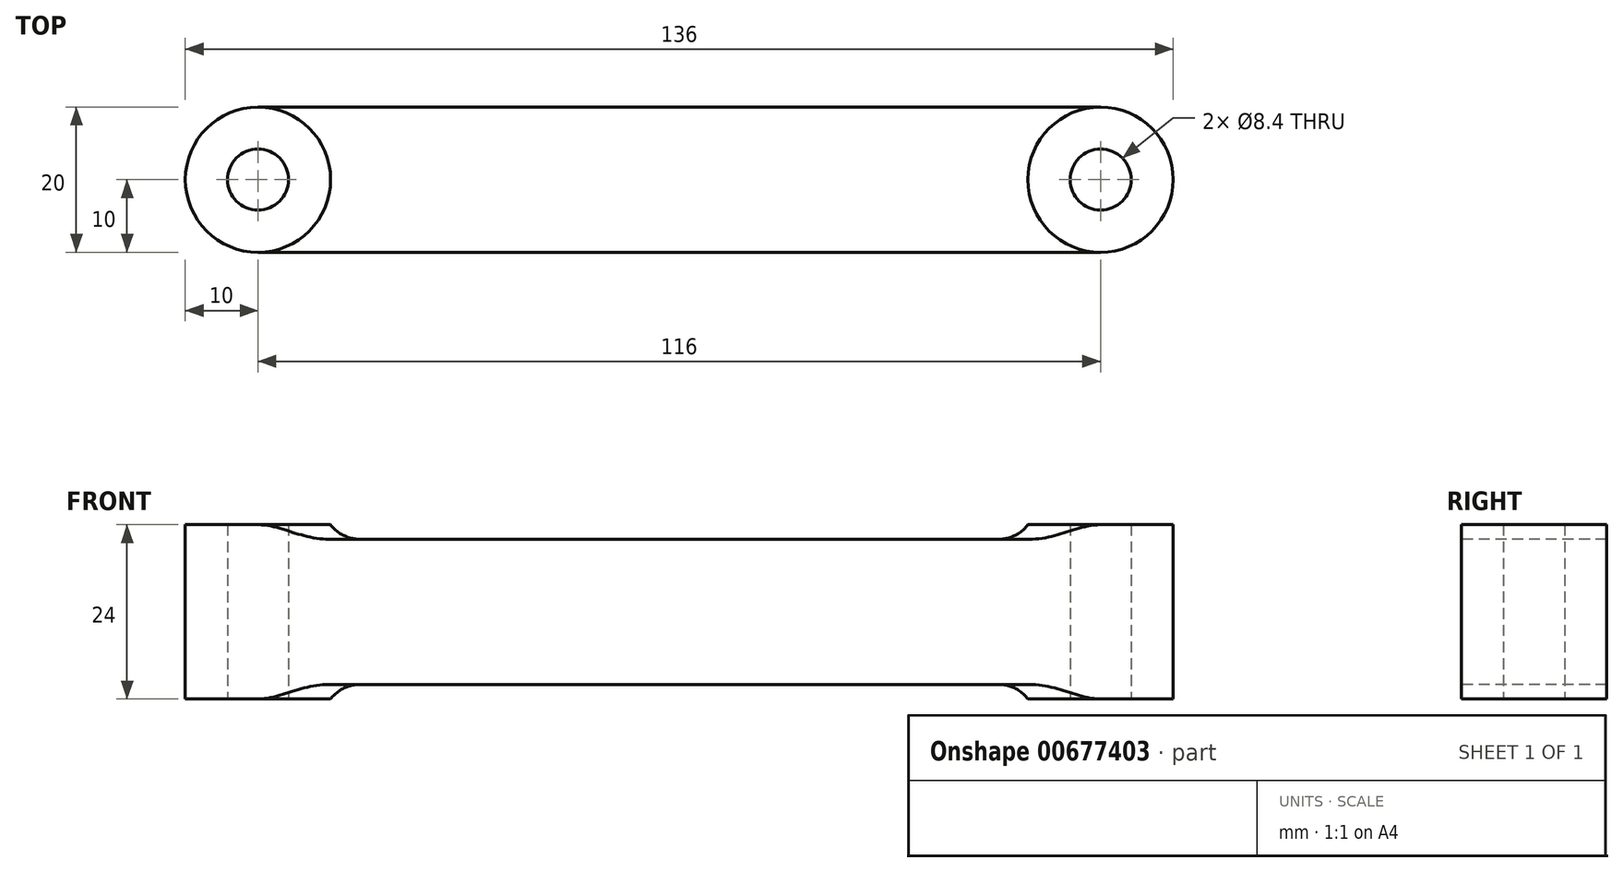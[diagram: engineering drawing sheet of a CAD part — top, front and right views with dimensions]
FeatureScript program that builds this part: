
annotation { "Feature Type Name" : "Feature", "Feature Type Description" : "" }
export const myFeature = defineFeature(function(context is Context, id is Id, definition is map)
    precondition{}
    {
        {
            var Q0;
            Q0=qCreatedBy(makeId("Top.planeOp"),FACE);
            var sketch = newSketch(context, id + "F0", { "sketchPlane" : qUnion([Q0])});
            skLineSegment(sketch, "E0.bottom", {"start": v(58, -10) * mm, "end": v(-58, -10) * mm});
            skLineSegment(sketch, "E0.top", {"start": v(58, 10) * mm, "end": v(-58, 10) * mm});
            skPoint(sketch, "E0.middle", {"position": v(0, 0) * mm});
            skCircle(sketch, "E1", {"center": v(-58, 0) * mm, "radius": 4.2 * mm});
            skPoint(sketch, "E1.centerSnap0", {"position": v(-68, 0) * mm});
            skCircle(sketch, "E2", {"center": v(58, 0) * mm, "radius": 4.2 * mm});
            skPoint(sketch, "E2.centerSnap0", {"position": v(68, 0) * mm});
            skArc(sketch, "E3", {"start": v(-58, 10) * mm, "mid": v(-68, 0) * mm, "end": v(-58, -10) * mm});
            skArc(sketch, "E4", {"start": v(58, -10) * mm, "mid": v(68, 0) * mm, "end": v(58, 10) * mm});
            skSolve(sketch);
        }
        {
            var Q0;
            Q0=makeQuery(id+"F0.imprint","IMPRINT",FACE,{"disambiguationData":[TD([[makeQuery(id+"F0.imprint","IMPRINT",EDGE,{"derivedFrom":sQuery(id+"F0.wireOp",EDGE,"E0.bottom")}),-1.0]])]});
            extrude(context, id + "F1", {"entities" : qUnion([Q0]), "depth" : 20 * mm, "offsetDistance" : 25 * mm});
        }
        {
            var Q0;
            Q0=makeQuery(id+"F1.opExtrude","CAP_FACE",FACE,{"disambiguationData":[OSD([sQuery(id+"F0.wireOp",EDGE,"E0.bottom"),sQuery(id+"F0.wireOp",EDGE,"E0.top"),sQuery(id+"F0.wireOp",EDGE,"E1"),sQuery(id+"F0.wireOp",EDGE,"E2"),sQuery(id+"F0.wireOp",EDGE,"E3"),sQuery(id+"F0.wireOp",EDGE,"E4")])],"isStart":false});
            var sketch = newSketch(context, id + "F2", { "sketchPlane" : qUnion([Q0])});
            skCircle(sketch, "E5", {"center": v(-58, 0) * mm, "radius": 10 * mm});
            skCircle(sketch, "E6", {"center": v(58, 0) * mm, "radius": 10 * mm});
            skCircle(sketch, "E7.0", {"center": v(-58, 0) * mm, "radius": 4.2 * mm});
            skCircle(sketch, "E8.0", {"center": v(58, 0) * mm, "radius": 4.2 * mm});
            skSolve(sketch);
        }
        {
            var Q0;
            Q0 = qSketchRegion(id + "F2", true);
            extrude(context, id + "F3", {"entities" : qUnion([Q0]), "operationType" : NewBodyOperationType.ADD, "depth" : 2 * mm, "offsetDistance" : 25 * mm, "hasSecondDirection" : true, "secondDirectionOppositeDirection" : true, "secondDirectionDepth" : 22 * mm});
        }
        {
            var Q0;
            Q0=makeQuery(id+"F3.boolean.opBoolean","INTERSECT",EDGE,{"derivedFrom":[makeQuery(id+"F1.opExtrude","CAP_FACE",FACE,{"disambiguationData":[OSD([sQuery(id+"F0.wireOp",EDGE,"E0.bottom"),sQuery(id+"F0.wireOp",EDGE,"E0.top"),sQuery(id+"F0.wireOp",EDGE,"E1"),sQuery(id+"F0.wireOp",EDGE,"E2"),sQuery(id+"F0.wireOp",EDGE,"E3"),sQuery(id+"F0.wireOp",EDGE,"E4")])],"isStart":false}),makeQuery(id+"F3.opExtrude","SWEPT_FACE",FACE,{"disambiguationData":[OSD([sQuery(id+"F2.wireOp",EDGE,"E5")])]})]});
            var Q1;
            Q1=makeQuery(id+"F3.boolean.opBoolean","INTERSECT",EDGE,{"derivedFrom":[makeQuery(id+"F1.opExtrude","CAP_FACE",FACE,{"disambiguationData":[OSD([sQuery(id+"F0.wireOp",EDGE,"E0.bottom"),sQuery(id+"F0.wireOp",EDGE,"E0.top"),sQuery(id+"F0.wireOp",EDGE,"E1"),sQuery(id+"F0.wireOp",EDGE,"E2"),sQuery(id+"F0.wireOp",EDGE,"E3"),sQuery(id+"F0.wireOp",EDGE,"E4")])],"isStart":true}),makeQuery(id+"F3.opExtrude","SWEPT_FACE",FACE,{"disambiguationData":[OSD([sQuery(id+"F2.wireOp",EDGE,"E5")])]})]});
            var Q2;
            Q2=makeQuery(id+"F3.boolean.opBoolean","INTERSECT",EDGE,{"derivedFrom":[makeQuery(id+"F1.opExtrude","CAP_FACE",FACE,{"disambiguationData":[OSD([sQuery(id+"F0.wireOp",EDGE,"E0.bottom"),sQuery(id+"F0.wireOp",EDGE,"E0.top"),sQuery(id+"F0.wireOp",EDGE,"E1"),sQuery(id+"F0.wireOp",EDGE,"E2"),sQuery(id+"F0.wireOp",EDGE,"E3"),sQuery(id+"F0.wireOp",EDGE,"E4")])],"isStart":false}),makeQuery(id+"F3.opExtrude","SWEPT_FACE",FACE,{"disambiguationData":[OSD([sQuery(id+"F2.wireOp",EDGE,"E6")])]})]});
            var Q3;
            Q3=makeQuery(id+"F3.boolean.opBoolean","INTERSECT",EDGE,{"derivedFrom":[makeQuery(id+"F1.opExtrude","CAP_FACE",FACE,{"disambiguationData":[OSD([sQuery(id+"F0.wireOp",EDGE,"E0.bottom"),sQuery(id+"F0.wireOp",EDGE,"E0.top"),sQuery(id+"F0.wireOp",EDGE,"E1"),sQuery(id+"F0.wireOp",EDGE,"E2"),sQuery(id+"F0.wireOp",EDGE,"E3"),sQuery(id+"F0.wireOp",EDGE,"E4")])],"isStart":true}),makeQuery(id+"F3.opExtrude","SWEPT_FACE",FACE,{"disambiguationData":[OSD([sQuery(id+"F2.wireOp",EDGE,"E6")])]})]});
            fillet(context, id + "F4", {"entities" : qUnion([Q0, Q1, Q2, Q3]), "radius" : 5 * mm, "tangentPropagation" : true, "allowEdgeOverflow" : false});
        }
    });
